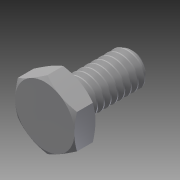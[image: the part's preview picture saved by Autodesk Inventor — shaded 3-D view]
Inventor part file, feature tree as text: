
AUTODESK INVENTOR PART (.ipt)
format: ipt  version: 2014 SP1 (Build 180222100, 222)  size: 441,344 bytes
history: native  units: in
note: dims shown in document units (in); Inventor stores cm internally (conversion verified against a paired STEP export)
features: extrude x1, other x1, imported_body x1
ambient origin geometry x8: Origin, YZ Plane, XZ Plane, XY Plane, X Axis, Y Axis, Z Axis, Center Point
bodies: Body1 (feature_tree)
feature tree (3):
  extrude  "Extrude14"  [1 undecoded]
  other  "92620A5371"
  imported_body  "Base1"
note: 1 required parameter value undecoded (feature->parameter linkage not recoverable at this tier; creation-order binding heuristic only, values carry confidence <= 0.55)
